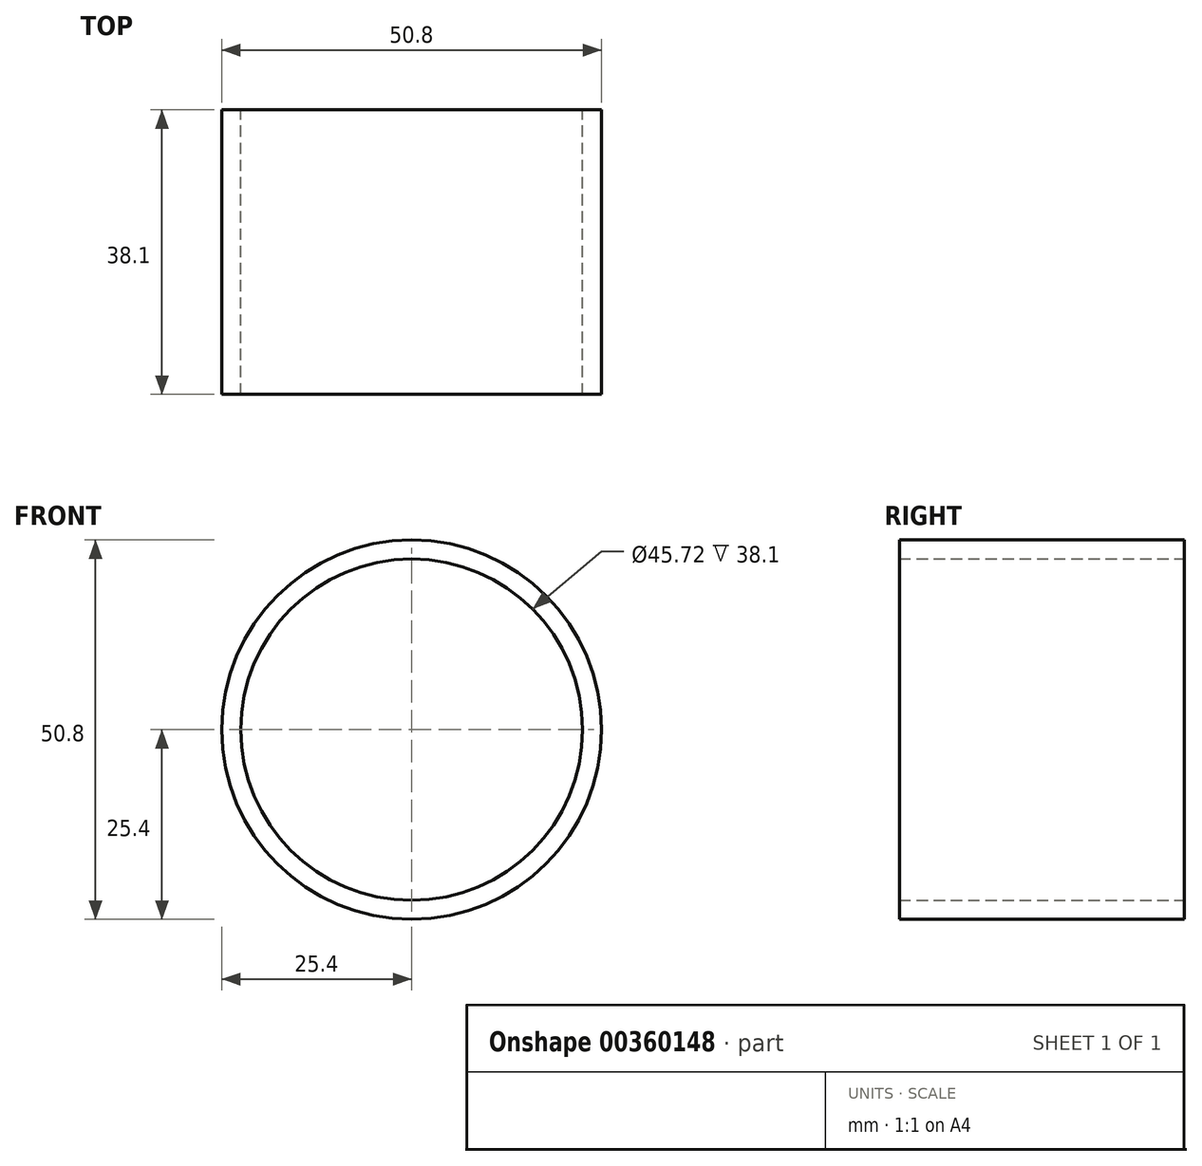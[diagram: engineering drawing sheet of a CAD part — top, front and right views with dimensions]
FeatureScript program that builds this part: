
annotation { "Feature Type Name" : "Feature", "Feature Type Description" : "" }
export const myFeature = defineFeature(function(context is Context, id is Id, definition is map)
    precondition{}
    {
        {
            var Q0;
            Q0=qCreatedBy(makeId("Front.planeOp"),FACE);
            var sketch = newSketch(context, id + "F0", { "sketchPlane" : qUnion([Q0])});
            skCircle(sketch, "E0", {"center": v(0, 0) * mm, "radius": 25.4 * mm});
            skCircle(sketch, "E1", {"center": v(0, 0) * mm, "radius": 22.86 * mm});
            skSolve(sketch);
        }
        {
            var Q0;
            Q0 = qSketchRegion(id + "F0", true);
            extrude(context, id + "F1", {"entities" : qUnion([Q0]), "depth" : 38.1 * mm});
        }
    });
